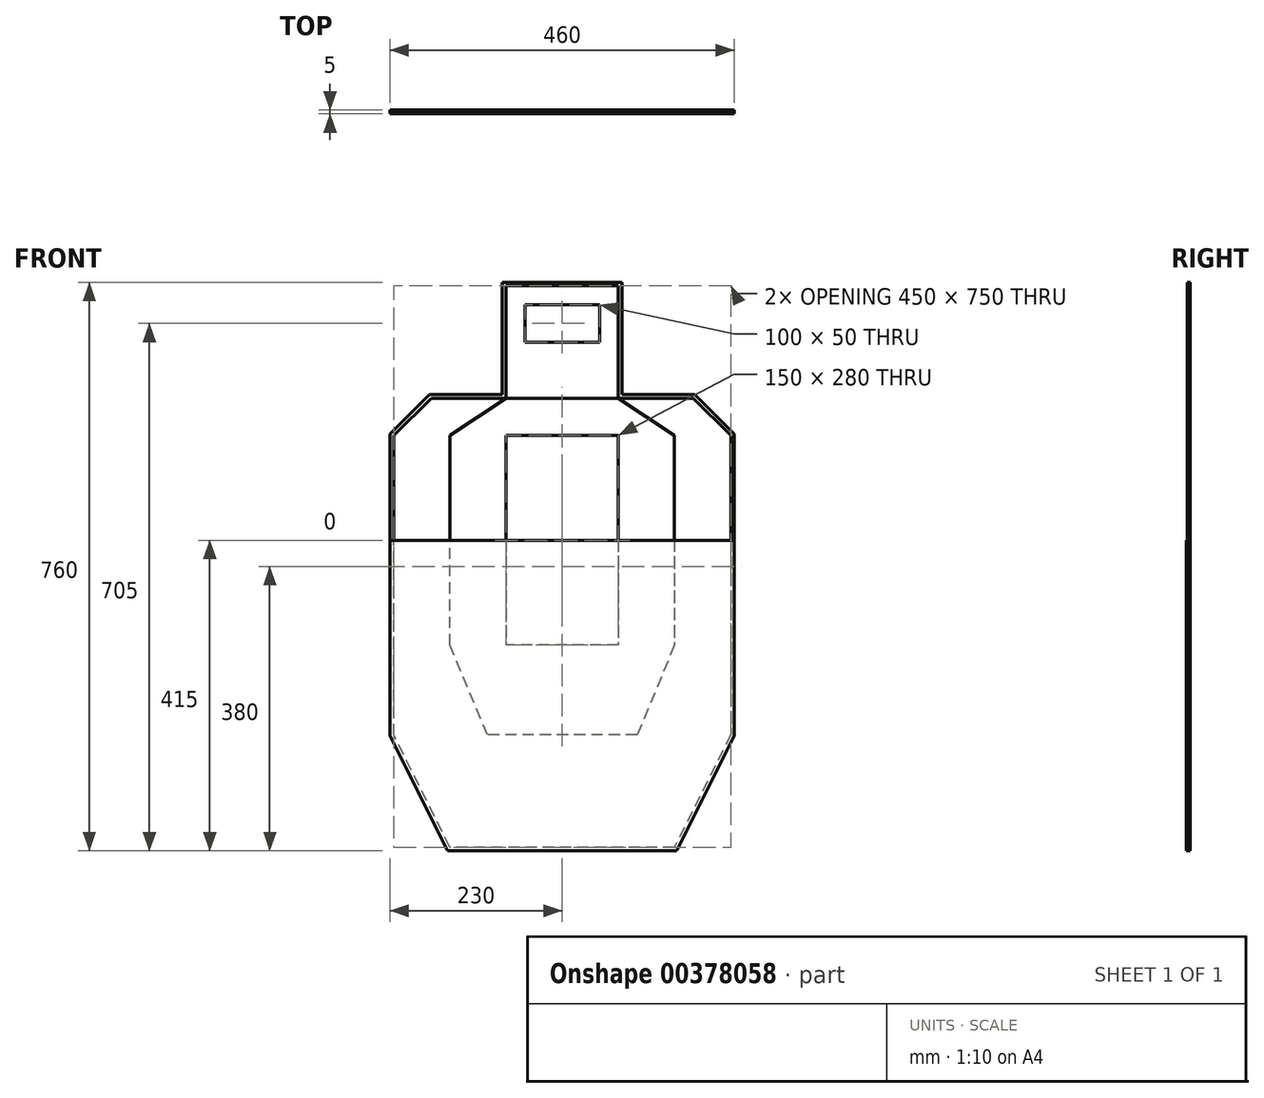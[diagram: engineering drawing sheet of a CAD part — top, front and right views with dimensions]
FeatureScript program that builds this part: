
annotation { "Feature Type Name" : "Feature", "Feature Type Description" : "" }
export const myFeature = defineFeature(function(context is Context, id is Id, definition is map)
    precondition{}
    {
        {
            var Q0;
            Q0=qCreatedBy(makeId("Front.planeOp"),FACE);
            var sketch = newSketch(context, id + "F0", { "sketchPlane" : qUnion([Q0])});
            skLineSegment(sketch, "E0.bottom", {"start": v(0, 100) * mm, "end": v(50, 100) * mm, "construction": true});
            skLineSegment(sketch, "E0.top", {"start": v(0, 125) * mm, "end": v(50, 125) * mm});
            skLineSegment(sketch, "E0.right", {"start": v(50, 100) * mm, "end": v(50, 125) * mm});
            skLineSegment(sketch, "E1.MirrorCS", {"start": v(0, 75) * mm, "end": v(50, 75) * mm});
            skLineSegment(sketch, "E2.MirrorCS", {"start": v(50, 100) * mm, "end": v(50, 75) * mm});
            skLineSegment(sketch, "E3.MirrorCS", {"start": v(0, 0) * mm, "end": v(0, 100) * mm, "construction": true});
            skLineSegment(sketch, "E4.MirrorCS", {"start": v(0, 125) * mm, "end": v(-50, 125) * mm});
            skLineSegment(sketch, "E5.MirrorCS", {"start": v(-50, 100) * mm, "end": v(-50, 125) * mm});
            skLineSegment(sketch, "E6.MirrorCS", {"start": v(-50, 100) * mm, "end": v(-50, 75) * mm});
            skLineSegment(sketch, "E7.MirrorCS", {"start": v(0, 75) * mm, "end": v(-50, 75) * mm});
            skSolve(sketch);
        }
        {
            var Q0;
            Q0=qSketchRegion(id+"F0",true);
            extrude(context, id + "F1", {"entities" : qUnion([Q0]), "oppositeDirection" : true, "depth" : 3 * mm});
        }
        {
            var Q0;
            Q0=qCreatedBy(makeId("Front.planeOp"),FACE);
            var sketch = newSketch(context, id + "F2", { "sketchPlane" : qUnion([Q0])});
            skLineSegment(sketch, "E8", {"start": v(75, 0) * mm, "end": v(75, 150) * mm});
            skLineSegment(sketch, "E9", {"start": v(75, 150) * mm, "end": v(-75, 150) * mm});
            skLineSegment(sketch, "E10", {"start": v(-75, 150) * mm, "end": v(-75, 0) * mm});
            skLineSegment(sketch, "E11", {"start": v(-75, 0) * mm, "end": v(75, 0) * mm});
            skLineSegment(sketch, "E12.0", {"start": v(0, 125) * mm, "end": v(-50, 125) * mm});
            skLineSegment(sketch, "E13.0", {"start": v(0, 125) * mm, "end": v(50, 125) * mm});
            skLineSegment(sketch, "E14.0", {"start": v(50, 100) * mm, "end": v(50, 125) * mm});
            skLineSegment(sketch, "E15.1", {"start": v(50, 100) * mm, "end": v(50, 75) * mm});
            skLineSegment(sketch, "E16.0", {"start": v(0, 75) * mm, "end": v(50, 75) * mm});
            skLineSegment(sketch, "E17.0", {"start": v(0, 75) * mm, "end": v(-50, 75) * mm});
            skLineSegment(sketch, "E18.0", {"start": v(-50, 100) * mm, "end": v(-50, 75) * mm});
            skLineSegment(sketch, "E19.1", {"start": v(-50, 100) * mm, "end": v(-50, 125) * mm});
            skLineSegment(sketch, "E20", {"start": v(0, 125) * mm, "end": v(0, 150) * mm, "construction": true});
            skLineSegment(sketch, "E21", {"start": v(0, 150) * mm, "end": v(0, 137.5) * mm, "construction": true});
            skSolve(sketch);
        }
        {
            var Q0;
            {var subQ0=sQuery(id+"F2.wireOp",EDGE,"E8");Q0=makeQuery(id+"F2.imprint","IMPRINT",FACE,{"disambiguationData":[TD([[makeQuery(id+"F2.imprint","IMPRINT",EDGE,{"derivedFrom":subQ0}),1.0]])]});}
            extrude(context, id + "F3", {"entities" : qUnion([Q0]), "oppositeDirection" : true, "depth" : 3 * mm});
        }
        {
            var Q0;
            Q0=qCreatedBy(makeId("Front.planeOp"),FACE);
            var sketch = newSketch(context, id + "F4", { "sketchPlane" : qUnion([Q0])});
            skLineSegment(sketch, "E22.bottom", {"start": v(75, -50) * mm, "end": v(-75, -50) * mm});
            skLineSegment(sketch, "E22.top", {"start": v(75, -330) * mm, "end": v(-75, -330) * mm});
            skLineSegment(sketch, "E22.left", {"start": v(75, -50) * mm, "end": v(75, -330) * mm});
            skLineSegment(sketch, "E22.right", {"start": v(-75, -50) * mm, "end": v(-75, -330) * mm});
            skLineSegment(sketch, "E23", {"start": v(0, 0) * mm, "end": v(0, -50) * mm, "construction": true});
            skLineSegment(sketch, "E24.0", {"start": v(-75, 0) * mm, "end": v(75, 0) * mm, "construction": true});
            skLineSegment(sketch, "E25", {"start": v(75, 0) * mm, "end": v(75, -50) * mm, "construction": true});
            skSolve(sketch);
        }
        {
            var Q0;
            Q0=makeQuery(id+"F4.imprint","IMPRINT",FACE,{"disambiguationData":[TD([[makeQuery(id+"F4.imprint","IMPRINT",EDGE,{"derivedFrom":sQuery(id+"F4.wireOp",EDGE,"E22.bottom")}),1.0]])]});
            extrude(context, id + "F5", {"entities" : qUnion([Q0]), "oppositeDirection" : true, "depth" : 3 * mm});
        }
        {
            var Q0;
            Q0=qCreatedBy(makeId("Front.planeOp"),FACE);
            var sketch = newSketch(context, id + "F6", { "sketchPlane" : qUnion([Q0])});
            skLineSegment(sketch, "E26.0", {"start": v(-75, 0) * mm, "end": v(75, 0) * mm});
            skLineSegment(sketch, "E27.1", {"start": v(75, -50) * mm, "end": v(75, -330) * mm});
            skLineSegment(sketch, "E28.2", {"start": v(75, -50) * mm, "end": v(-75, -50) * mm});
            skLineSegment(sketch, "E29.3", {"start": v(-75, -50) * mm, "end": v(-75, -330) * mm});
            skLineSegment(sketch, "E30.0", {"start": v(75, -330) * mm, "end": v(-75, -330) * mm});
            skLineSegment(sketch, "E31", {"start": v(75, 0) * mm, "end": v(150, -50) * mm});
            skLineSegment(sketch, "E32", {"start": v(150, -50) * mm, "end": v(150, -330) * mm});
            skLineSegment(sketch, "E33", {"start": v(150, -330) * mm, "end": v(100, -450) * mm});
            skLineSegment(sketch, "E34", {"start": v(100, -450) * mm, "end": v(-100, -450) * mm});
            skLineSegment(sketch, "E35", {"start": v(-100, -450) * mm, "end": v(-150, -330) * mm});
            skLineSegment(sketch, "E36", {"start": v(-150, -330) * mm, "end": v(-150, -50) * mm});
            skLineSegment(sketch, "E37", {"start": v(-150, -50) * mm, "end": v(-75, 0) * mm});
            skLineSegment(sketch, "E38", {"start": v(0, -450) * mm, "end": v(0, -50) * mm, "construction": true});
            skLineSegment(sketch, "E39", {"start": v(150, -50) * mm, "end": v(75, -50) * mm, "construction": true});
            skLineSegment(sketch, "E40", {"start": v(-55.04, -50) * mm, "end": v(-150, -50) * mm, "construction": true});
            skLineSegment(sketch, "E41", {"start": v(150, -330) * mm, "end": v(150, -450) * mm, "construction": true});
            skLineSegment(sketch, "E42", {"start": v(100, -450) * mm, "end": v(150, -450) * mm, "construction": true});
            skLineSegment(sketch, "E43", {"start": v(150, -330) * mm, "end": v(-150, -330) * mm, "construction": true});
            skLineSegment(sketch, "E44", {"start": v(-150, -330) * mm, "end": v(-150, -450) * mm, "construction": true});
            skLineSegment(sketch, "E45", {"start": v(-150, -450) * mm, "end": v(-100, -450) * mm, "construction": true});
            skSolve(sketch);
        }
        {
            var Q0;
            Q0=makeQuery(id+"F6.imprint","IMPRINT",FACE,{"disambiguationData":[TD([[makeQuery(id+"F6.imprint","IMPRINT",EDGE,{"derivedFrom":sQuery(id+"F6.wireOp",EDGE,"E26.0")}),-1.0]])]});
            extrude(context, id + "F7", {"entities" : qUnion([Q0]), "oppositeDirection" : true, "depth" : 3 * mm});
        }
        {
            var Q0;
            Q0=makeQuery(id+"F7.opExtrude","CAP_FACE",FACE,{"disambiguationData":[OSD([sQuery(id+"F6.wireOp",EDGE,"E26.0"),sQuery(id+"F6.wireOp",EDGE,"E27.1"),sQuery(id+"F6.wireOp",EDGE,"E28.2"),sQuery(id+"F6.wireOp",EDGE,"E29.3"),sQuery(id+"F6.wireOp",EDGE,"E30.0"),sQuery(id+"F6.wireOp",EDGE,"E31"),sQuery(id+"F6.wireOp",EDGE,"E32"),sQuery(id+"F6.wireOp",EDGE,"E33"),sQuery(id+"F6.wireOp",EDGE,"E34"),sQuery(id+"F6.wireOp",EDGE,"E35"),sQuery(id+"F6.wireOp",EDGE,"E36"),sQuery(id+"F6.wireOp",EDGE,"E37")])],"isStart":true});
            var sketch = newSketch(context, id + "F8", { "sketchPlane" : qUnion([Q0])});
            skLineSegment(sketch, "E46.0", {"start": v(75, 0) * mm, "end": v(150, -50) * mm});
            skLineSegment(sketch, "E47.0", {"start": v(150, -50) * mm, "end": v(150, -330) * mm});
            skLineSegment(sketch, "E48.0", {"start": v(150, -330) * mm, "end": v(100, -450) * mm});
            skLineSegment(sketch, "E49.1", {"start": v(100, -450) * mm, "end": v(-100, -450) * mm});
            skLineSegment(sketch, "E50.0", {"start": v(-150, -330) * mm, "end": v(-150, -50) * mm});
            skLineSegment(sketch, "E51.0", {"start": v(-100, -450) * mm, "end": v(-150, -330) * mm});
            skLineSegment(sketch, "E52.0", {"start": v(-150, -50) * mm, "end": v(-75, 0) * mm});
            skLineSegment(sketch, "E53", {"start": v(75, 0) * mm, "end": v(175, 0) * mm});
            skLineSegment(sketch, "E54", {"start": v(175, 0) * mm, "end": v(225, -50) * mm});
            skLineSegment(sketch, "E55", {"start": v(225, -50) * mm, "end": v(225, -450) * mm});
            skLineSegment(sketch, "E56", {"start": v(225, -450) * mm, "end": v(150, -600) * mm});
            skLineSegment(sketch, "E57", {"start": v(150, -600) * mm, "end": v(-150, -600) * mm});
            skLineSegment(sketch, "E58", {"start": v(-150, -600) * mm, "end": v(-225, -450) * mm});
            skLineSegment(sketch, "E59", {"start": v(-225, -450) * mm, "end": v(-225, -50) * mm});
            skLineSegment(sketch, "E60", {"start": v(-225, -50) * mm, "end": v(-175, 0) * mm});
            skLineSegment(sketch, "E61", {"start": v(-175, 0) * mm, "end": v(-75, 0) * mm});
            skLineSegment(sketch, "E62", {"start": v(225, -50) * mm, "end": v(225, 0) * mm, "construction": true});
            skLineSegment(sketch, "E63", {"start": v(225, 0) * mm, "end": v(175, 0) * mm, "construction": true});
            skLineSegment(sketch, "E64", {"start": v(225, -450) * mm, "end": v(225, -600) * mm, "construction": true});
            skLineSegment(sketch, "E65", {"start": v(225, -600) * mm, "end": v(150, -600) * mm, "construction": true});
            skLineSegment(sketch, "E66", {"start": v(-225, -450) * mm, "end": v(-225, -600) * mm, "construction": true});
            skLineSegment(sketch, "E67", {"start": v(-225, -600) * mm, "end": v(-150, -600) * mm, "construction": true});
            skLineSegment(sketch, "E68", {"start": v(-175, 0) * mm, "end": v(-225, 0) * mm, "construction": true});
            skLineSegment(sketch, "E69", {"start": v(-225, 0) * mm, "end": v(-225, -50) * mm, "construction": true});
            skSolve(sketch);
        }
        {
            var Q0;
            Q0=qSketchRegion(id+"F8",true);
            extrude(context, id + "F9", {"entities" : qUnion([Q0]), "oppositeDirection" : true, "depth" : 3 * mm});
        }
        {
            var Q0;
            Q0=makeQuery(id+"F9.opExtrude","CAP_FACE",FACE,{"disambiguationData":[OSD([sQuery(id+"F8.wireOp",EDGE,"E46.0"),sQuery(id+"F8.wireOp",EDGE,"E47.0"),sQuery(id+"F8.wireOp",EDGE,"E48.0"),sQuery(id+"F8.wireOp",EDGE,"E49.1"),sQuery(id+"F8.wireOp",EDGE,"E50.0"),sQuery(id+"F8.wireOp",EDGE,"E51.0"),sQuery(id+"F8.wireOp",EDGE,"E52.0"),sQuery(id+"F8.wireOp",EDGE,"E53"),sQuery(id+"F8.wireOp",EDGE,"E54"),sQuery(id+"F8.wireOp",EDGE,"E55"),sQuery(id+"F8.wireOp",EDGE,"E56"),sQuery(id+"F8.wireOp",EDGE,"E57"),sQuery(id+"F8.wireOp",EDGE,"E58"),sQuery(id+"F8.wireOp",EDGE,"E59"),sQuery(id+"F8.wireOp",EDGE,"E60"),sQuery(id+"F8.wireOp",EDGE,"E61")])],"isStart":true});
            var sketch = newSketch(context, id + "F10", { "sketchPlane" : qUnion([Q0])});
            skLineSegment(sketch, "E70.0", {"start": v(75, 150) * mm, "end": v(-75, 150) * mm});
            skLineSegment(sketch, "E71.0", {"start": v(75, 0) * mm, "end": v(75, 150) * mm});
            skLineSegment(sketch, "E72.1", {"start": v(75, 0) * mm, "end": v(175, 0) * mm});
            skLineSegment(sketch, "E73.0", {"start": v(175, 0) * mm, "end": v(225, -50) * mm});
            skLineSegment(sketch, "E74.1", {"start": v(225, -50) * mm, "end": v(225, -450) * mm});
            skLineSegment(sketch, "E75.0", {"start": v(225, -450) * mm, "end": v(150, -600) * mm});
            skLineSegment(sketch, "E76.1", {"start": v(150, -600) * mm, "end": v(-150, -600) * mm});
            skLineSegment(sketch, "E77.2", {"start": v(-150, -600) * mm, "end": v(-225, -450) * mm});
            skLineSegment(sketch, "E78.3", {"start": v(-225, -450) * mm, "end": v(-225, -50) * mm});
            skLineSegment(sketch, "E79.4", {"start": v(-225, -50) * mm, "end": v(-175, 0) * mm});
            skLineSegment(sketch, "E80.5", {"start": v(-175, 0) * mm, "end": v(-75, 0) * mm});
            skLineSegment(sketch, "E81.0", {"start": v(-75, 150) * mm, "end": v(-75, 0) * mm});
            skLineSegment(sketch, "E82.0", {"start": v(177.07, 5) * mm, "end": v(230, -47.93) * mm});
            skLineSegment(sketch, "E82.1", {"start": v(-230, -451.18) * mm, "end": v(-230, -47.93) * mm});
            skLineSegment(sketch, "E82.2", {"start": v(-153.1, -605) * mm, "end": v(-230, -451.18) * mm});
            skLineSegment(sketch, "E82.3", {"start": v(153.1, -605) * mm, "end": v(-153.1, -605) * mm});
            skLineSegment(sketch, "E82.4", {"start": v(230, -451.18) * mm, "end": v(153.1, -605) * mm});
            skLineSegment(sketch, "E82.5", {"start": v(-230, -47.93) * mm, "end": v(-177.07, 5) * mm});
            skLineSegment(sketch, "E82.6", {"start": v(230, -47.93) * mm, "end": v(230, -451.18) * mm});
            skLineSegment(sketch, "E82.7", {"start": v(-177.07, 5) * mm, "end": v(-80, 5) * mm});
            skLineSegment(sketch, "E82.8", {"start": v(-80, 155) * mm, "end": v(-80, 5) * mm});
            skLineSegment(sketch, "E82.9", {"start": v(80, 155) * mm, "end": v(-80, 155) * mm});
            skLineSegment(sketch, "E82.10", {"start": v(80, 5) * mm, "end": v(80, 155) * mm});
            skLineSegment(sketch, "E82.11", {"start": v(80, 5) * mm, "end": v(177.07, 5) * mm});
            skSolve(sketch);
        }
        {
            var Q0;
            Q0=makeQuery(id+"F10.imprint","IMPRINT",FACE,{"disambiguationData":[TD([[makeQuery(id+"F10.imprint","IMPRINT",EDGE,{"derivedFrom":sQuery(id+"F10.wireOp",EDGE,"E70.0")}),-1.0]])]});
            extrude(context, id + "F11", {"entities" : qUnion([Q0]), "oppositeDirection" : true, "depth" : 3 * mm});
        }
        {
            var Q0;
            Q0=makeQuery(id+"F9.opExtrude","CAP_FACE",FACE,{"disambiguationData":[OSD([sQuery(id+"F8.wireOp",EDGE,"E46.0"),sQuery(id+"F8.wireOp",EDGE,"E47.0"),sQuery(id+"F8.wireOp",EDGE,"E48.0"),sQuery(id+"F8.wireOp",EDGE,"E49.1"),sQuery(id+"F8.wireOp",EDGE,"E50.0"),sQuery(id+"F8.wireOp",EDGE,"E51.0"),sQuery(id+"F8.wireOp",EDGE,"E52.0"),sQuery(id+"F8.wireOp",EDGE,"E53"),sQuery(id+"F8.wireOp",EDGE,"E54"),sQuery(id+"F8.wireOp",EDGE,"E55"),sQuery(id+"F8.wireOp",EDGE,"E56"),sQuery(id+"F8.wireOp",EDGE,"E57"),sQuery(id+"F8.wireOp",EDGE,"E58"),sQuery(id+"F8.wireOp",EDGE,"E59"),sQuery(id+"F8.wireOp",EDGE,"E60"),sQuery(id+"F8.wireOp",EDGE,"E61")])],"isStart":false});
            var sketch = newSketch(context, id + "F12", { "sketchPlane" : qUnion([Q0])});
            skLineSegment(sketch, "E83.0", {"start": v(75, 150) * mm, "end": v(75, 0) * mm});
            skLineSegment(sketch, "E84.0", {"start": v(175, 0) * mm, "end": v(75, 0) * mm});
            skLineSegment(sketch, "E85.0", {"start": v(-75, 150) * mm, "end": v(75, 150) * mm});
            skLineSegment(sketch, "E86.0", {"start": v(225, -50) * mm, "end": v(175, 0) * mm});
            skLineSegment(sketch, "E87.0", {"start": v(-225, -50) * mm, "end": v(-225, -450) * mm});
            skLineSegment(sketch, "E87.1", {"start": v(225, -450) * mm, "end": v(225, -50) * mm});
            skLineSegment(sketch, "E87.2", {"start": v(150, -600) * mm, "end": v(225, -450) * mm});
            skLineSegment(sketch, "E87.3", {"start": v(-225, -450) * mm, "end": v(-150, -600) * mm});
            skLineSegment(sketch, "E87.4", {"start": v(-150, -600) * mm, "end": v(150, -600) * mm});
            skLineSegment(sketch, "E88.0", {"start": v(-175, 0) * mm, "end": v(-225, -50) * mm});
            skLineSegment(sketch, "E89.0", {"start": v(-75, 0) * mm, "end": v(-175, 0) * mm});
            skLineSegment(sketch, "E90.0", {"start": v(-75, 0) * mm, "end": v(-75, 150) * mm});
            skSolve(sketch);
        }
        {
            var Q0;
            Q0=qSketchRegion(id+"F12",true);
            extrude(context, id + "F13", {"entities" : qUnion([Q0]), "depth" : 1 * mm});
        }
        {
            var Q0;
            Q0=makeQuery(id+"F13.opExtrude","CAP_FACE",FACE,{"disambiguationData":[OSD([sQuery(id+"F12.wireOp",EDGE,"E83.0"),sQuery(id+"F12.wireOp",EDGE,"E84.0"),sQuery(id+"F12.wireOp",EDGE,"E85.0"),sQuery(id+"F12.wireOp",EDGE,"E86.0"),sQuery(id+"F12.wireOp",EDGE,"E87.0"),sQuery(id+"F12.wireOp",EDGE,"E87.1"),sQuery(id+"F12.wireOp",EDGE,"E87.2"),sQuery(id+"F12.wireOp",EDGE,"E87.3"),sQuery(id+"F12.wireOp",EDGE,"E87.4"),sQuery(id+"F12.wireOp",EDGE,"E88.0"),sQuery(id+"F12.wireOp",EDGE,"E89.0"),sQuery(id+"F12.wireOp",EDGE,"E90.0")])],"isStart":false});
            var sketch = newSketch(context, id + "F14", { "sketchPlane" : qUnion([Q0])});
            skLineSegment(sketch, "E91.0", {"start": v(-80, 155) * mm, "end": v(80, 155) * mm});
            skLineSegment(sketch, "E92.0", {"start": v(80, 155) * mm, "end": v(80, 5) * mm});
            skLineSegment(sketch, "E93.0", {"start": v(-80, 5) * mm, "end": v(-80, 155) * mm});
            skLineSegment(sketch, "E94.0", {"start": v(177.07, 5) * mm, "end": v(80, 5) * mm});
            skLineSegment(sketch, "E95.0", {"start": v(-80, 5) * mm, "end": v(-177.07, 5) * mm});
            skLineSegment(sketch, "E96.0", {"start": v(230, -47.93) * mm, "end": v(177.07, 5) * mm});
            skLineSegment(sketch, "E97.0", {"start": v(-177.07, 5) * mm, "end": v(-230, -47.93) * mm});
            skLineSegment(sketch, "E98.1", {"start": v(-230, -47.93) * mm, "end": v(-230, -451.18) * mm});
            skLineSegment(sketch, "E99.0", {"start": v(-230, -451.18) * mm, "end": v(-153.1, -605) * mm});
            skLineSegment(sketch, "E100.0", {"start": v(-153.1, -605) * mm, "end": v(153.1, -605) * mm});
            skLineSegment(sketch, "E101.0", {"start": v(153.1, -605) * mm, "end": v(230, -451.18) * mm});
            skLineSegment(sketch, "E102.0", {"start": v(230, -451.18) * mm, "end": v(230, -47.93) * mm});
            skLineSegment(sketch, "E103.0", {"start": v(-75, 150) * mm, "end": v(75, 150) * mm});
            skLineSegment(sketch, "E104.0", {"start": v(-75, 0) * mm, "end": v(-75, 150) * mm});
            skLineSegment(sketch, "E105.0", {"start": v(75, 150) * mm, "end": v(75, 0) * mm});
            skLineSegment(sketch, "E106.0", {"start": v(175, 0) * mm, "end": v(75, 0) * mm});
            skLineSegment(sketch, "E107.0", {"start": v(225, -50) * mm, "end": v(175, 0) * mm});
            skLineSegment(sketch, "E108.0", {"start": v(150, -600) * mm, "end": v(225, -450) * mm});
            skLineSegment(sketch, "E109.0", {"start": v(225, -450) * mm, "end": v(225, -50) * mm});
            skLineSegment(sketch, "E110.0", {"start": v(-150, -600) * mm, "end": v(150, -600) * mm});
            skLineSegment(sketch, "E111.0", {"start": v(-225, -450) * mm, "end": v(-150, -600) * mm});
            skLineSegment(sketch, "E112.0", {"start": v(-225, -50) * mm, "end": v(-225, -450) * mm});
            skLineSegment(sketch, "E113.0", {"start": v(-175, 0) * mm, "end": v(-225, -50) * mm});
            skLineSegment(sketch, "E114.0", {"start": v(-75, 0) * mm, "end": v(-175, 0) * mm});
            skSolve(sketch);
        }
        {
            var Q0;
            Q0=makeQuery(id+"F14.imprint","IMPRINT",FACE,{"disambiguationData":[TD([[makeQuery(id+"F14.imprint","IMPRINT",EDGE,{"derivedFrom":sQuery(id+"F14.wireOp",EDGE,"E91.0")}),-1.0]])]});
            extrude(context, id + "F15", {"entities" : qUnion([Q0]), "oppositeDirection" : true, "depth" : 1 * mm});
        }
        {
            var Q0;
            Q0=makeQuery(id+"F9.opExtrude","CAP_FACE",FACE,{"disambiguationData":[OSD([sQuery(id+"F8.wireOp",EDGE,"E46.0"),sQuery(id+"F8.wireOp",EDGE,"E47.0"),sQuery(id+"F8.wireOp",EDGE,"E48.0"),sQuery(id+"F8.wireOp",EDGE,"E49.1"),sQuery(id+"F8.wireOp",EDGE,"E50.0"),sQuery(id+"F8.wireOp",EDGE,"E51.0"),sQuery(id+"F8.wireOp",EDGE,"E52.0"),sQuery(id+"F8.wireOp",EDGE,"E53"),sQuery(id+"F8.wireOp",EDGE,"E54"),sQuery(id+"F8.wireOp",EDGE,"E55"),sQuery(id+"F8.wireOp",EDGE,"E56"),sQuery(id+"F8.wireOp",EDGE,"E57"),sQuery(id+"F8.wireOp",EDGE,"E58"),sQuery(id+"F8.wireOp",EDGE,"E59"),sQuery(id+"F8.wireOp",EDGE,"E60"),sQuery(id+"F8.wireOp",EDGE,"E61")])],"isStart":true});
            var sketch = newSketch(context, id + "F16", { "sketchPlane" : qUnion([Q0])});
            skLineSegment(sketch, "E115.0", {"start": v(-153.1, -605) * mm, "end": v(-230, -451.18) * mm});
            skLineSegment(sketch, "E116.0", {"start": v(-230, -451.18) * mm, "end": v(-230, -190) * mm});
            skLineSegment(sketch, "E117.0", {"start": v(153.1, -605) * mm, "end": v(-153.1, -605) * mm});
            skLineSegment(sketch, "E118.0", {"start": v(230, -451.18) * mm, "end": v(153.1, -605) * mm});
            skLineSegment(sketch, "E119.0", {"start": v(230, -190) * mm, "end": v(230, -451.18) * mm});
            skLineSegment(sketch, "E120.0", {"start": v(-75, -50) * mm, "end": v(-75, -330) * mm, "construction": true});
            skLineSegment(sketch, "E121.0", {"start": v(75, -50) * mm, "end": v(75, -330) * mm, "construction": true});
            skLineSegment(sketch, "E122", {"start": v(230, -190) * mm, "end": v(-230, -190) * mm});
            skPoint(sketch, "E123.orphan", {"position": v(-75, -190) * mm});
            skSolve(sketch);
        }
        {
            var Q0;
            Q0=qSketchRegion(id+"F16",true);
            extrude(context, id + "F17", {"entities" : qUnion([Q0]), "depth" : 1 * mm});
        }
    });
